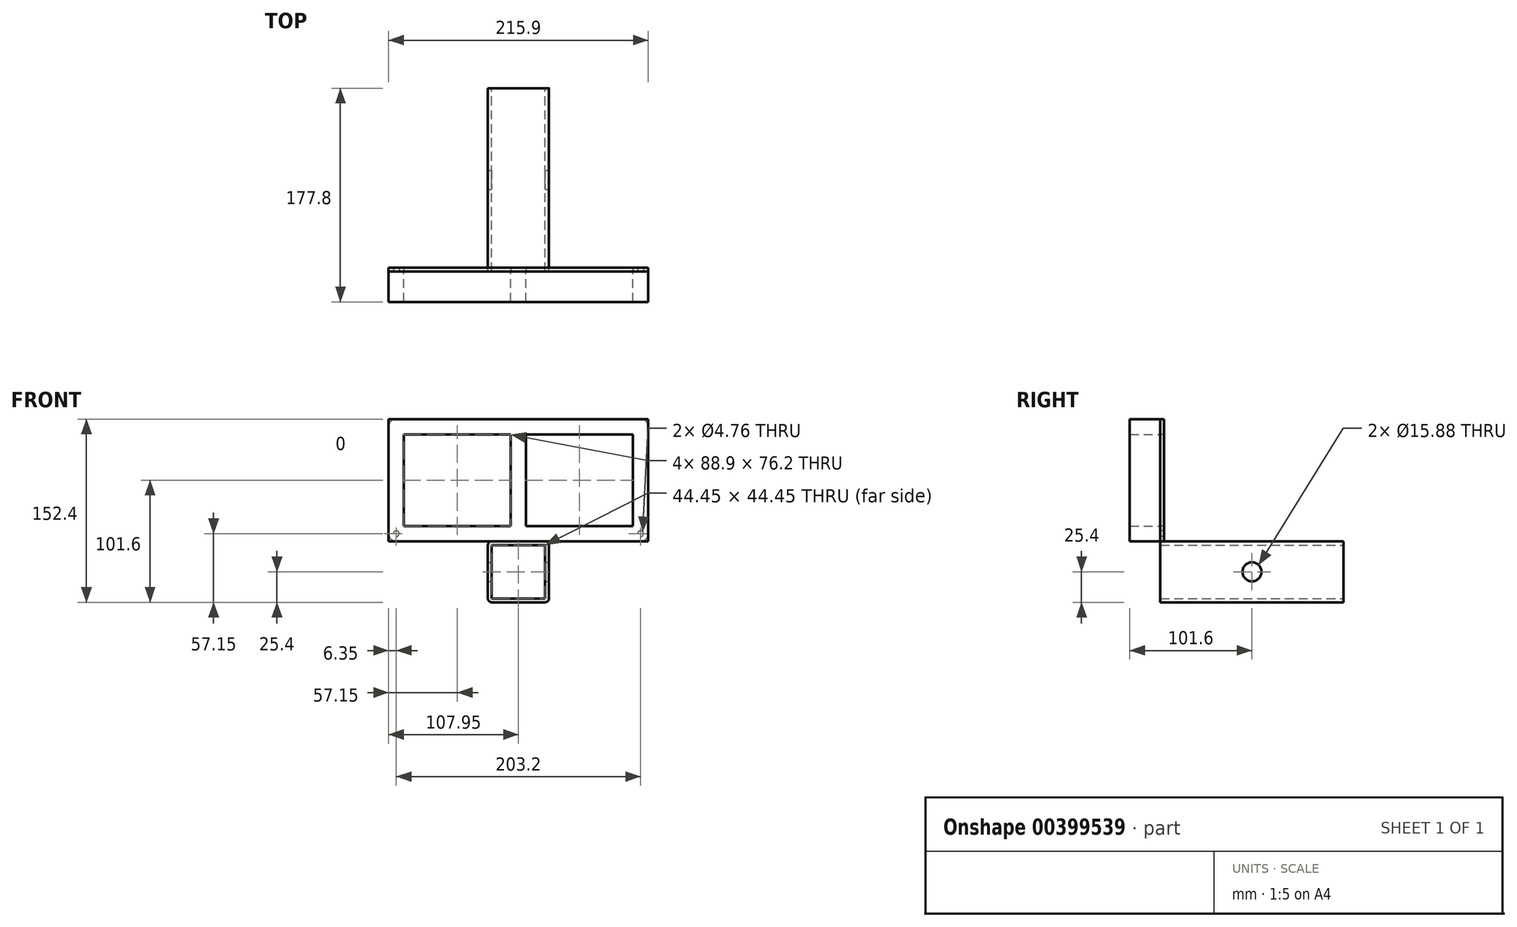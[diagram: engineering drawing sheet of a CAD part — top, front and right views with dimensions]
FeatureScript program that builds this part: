
annotation { "Feature Type Name" : "Feature", "Feature Type Description" : "" }
export const myFeature = defineFeature(function(context is Context, id is Id, definition is map)
    precondition{}
    {
        {
            var Q0;
            Q0=qCreatedBy(makeId("Front.planeOp"),FACE);
            var sketch = newSketch(context, id + "F0", { "sketchPlane" : qUnion([Q0])});
            skLineSegment(sketch, "E0.bottom", {"start": v(22.23, 25.4) * mm, "end": v(-22.23, 25.4) * mm});
            skLineSegment(sketch, "E0.top", {"start": v(22.23, -25.4) * mm, "end": v(-22.23, -25.4) * mm});
            skLineSegment(sketch, "E0.left", {"start": v(25.4, 22.23) * mm, "end": v(25.4, -22.22) * mm});
            skLineSegment(sketch, "E0.right", {"start": v(-25.4, 22.23) * mm, "end": v(-25.4, -22.23) * mm});
            skPoint(sketch, "E0.middle", {"position": v(0, 0) * mm});
            skLineSegment(sketch, "E1.0", {"start": v(22.23, 22.23) * mm, "end": v(-22.23, 22.23) * mm});
            skLineSegment(sketch, "E1.1", {"start": v(22.23, 22.23) * mm, "end": v(22.23, -22.22) * mm});
            skLineSegment(sketch, "E1.2", {"start": v(22.23, -22.22) * mm, "end": v(-22.23, -22.22) * mm});
            skLineSegment(sketch, "E1.3", {"start": v(-22.23, 22.23) * mm, "end": v(-22.23, -22.23) * mm});
            skPoint(sketch, "E2.visualSharp", {"position": v(-25.4, 25.4) * mm});
            skArc(sketch, "E2.filletArc", {"start": v(-22.23, 25.4) * mm, "mid": v(-24.47, 24.47) * mm, "end": v(-25.4, 22.23) * mm});
            skPoint(sketch, "E3.visualSharp", {"position": v(25.4, 25.4) * mm});
            skArc(sketch, "E3.filletArc", {"start": v(25.4, 22.23) * mm, "mid": v(24.47, 24.47) * mm, "end": v(22.23, 25.4) * mm});
            skPoint(sketch, "E4.visualSharp", {"position": v(25.4, -25.4) * mm});
            skArc(sketch, "E4.filletArc", {"start": v(22.23, -25.4) * mm, "mid": v(24.47, -24.47) * mm, "end": v(25.4, -22.22) * mm});
            skPoint(sketch, "E5.visualSharp", {"position": v(-25.4, -25.4) * mm});
            skArc(sketch, "E5.filletArc", {"start": v(-25.4, -22.23) * mm, "mid": v(-24.47, -24.47) * mm, "end": v(-22.23, -25.4) * mm});
            skSolve(sketch);
        }
        {
            var Q0;
            Q0=makeQuery(id+"F0.imprint","IMPRINT",FACE,{"disambiguationData":[TD([[makeQuery(id+"F0.imprint","IMPRINT",EDGE,{"derivedFrom":sQuery(id+"F0.wireOp",EDGE,"E0.bottom")}),1.0]])]});
            extrude(context, id + "F1", {"entities" : qUnion([Q0]), "depth" : 152.4 * mm});
        }
        {
            var Q0;
            Q0=makeQuery(id+"F1.opExtrude","SWEPT_FACE",FACE,{"disambiguationData":[OSD([sQuery(id+"F0.wireOp",EDGE,"E0.left")])]});
            var sketch = newSketch(context, id + "F2", { "sketchPlane" : qUnion([Q0])});
            skLineSegment(sketch, "E6", {"start": v(-152.4, 0) * mm, "end": v(-76.2, 0) * mm});
            skSolve(sketch);
        }
        {
            var Q0;
            Q0=sQuery(id+"F2.wireOp",VERTEX,"E6.end");
            var Q1;
            Q1=makeQuery(id+"F1.opExtrude","SWEPT_BODY",BODY,{"disambiguationData":[OSD([sQuery(id+"F0.wireOp",EDGE,"E0.bottom"),sQuery(id+"F0.wireOp",EDGE,"E0.top"),sQuery(id+"F0.wireOp",EDGE,"E0.left"),sQuery(id+"F0.wireOp",EDGE,"E0.right"),sQuery(id+"F0.wireOp",EDGE,"E1.0"),sQuery(id+"F0.wireOp",EDGE,"E1.1"),sQuery(id+"F0.wireOp",EDGE,"E1.2"),sQuery(id+"F0.wireOp",EDGE,"E1.3"),sQuery(id+"F0.wireOp",EDGE,"E2.filletArc"),sQuery(id+"F0.wireOp",EDGE,"E3.filletArc"),sQuery(id+"F0.wireOp",EDGE,"E4.filletArc"),sQuery(id+"F0.wireOp",EDGE,"E5.filletArc")])]});
            hole(context, id + "F3", {"style" : HoleStyle.SIMPLE, "endStyle" : HoleEndStyle.THROUGH, "holeDiameter" : 15.88 * mm, "locations" : qUnion([Q0]), "scope" : qUnion([Q1]), "isTappedThrough" : true});
        }
        {
            var Q0;
            Q0=makeQuery(id+"F1.opExtrude","CAP_FACE",FACE,{"disambiguationData":[OSD([sQuery(id+"F0.wireOp",EDGE,"E0.bottom"),sQuery(id+"F0.wireOp",EDGE,"E0.top"),sQuery(id+"F0.wireOp",EDGE,"E0.left"),sQuery(id+"F0.wireOp",EDGE,"E0.right"),sQuery(id+"F0.wireOp",EDGE,"E1.0"),sQuery(id+"F0.wireOp",EDGE,"E1.1"),sQuery(id+"F0.wireOp",EDGE,"E1.2"),sQuery(id+"F0.wireOp",EDGE,"E1.3"),sQuery(id+"F0.wireOp",EDGE,"E2.filletArc"),sQuery(id+"F0.wireOp",EDGE,"E3.filletArc"),sQuery(id+"F0.wireOp",EDGE,"E4.filletArc"),sQuery(id+"F0.wireOp",EDGE,"E5.filletArc")])],"isStart":false});
            var sketch = newSketch(context, id + "F4", { "sketchPlane" : qUnion([Q0])});
            skLineSegment(sketch, "E7", {"start": v(0, -1) * mm, "end": v(0, 25.4) * mm});
            skLineSegment(sketch, "E8", {"start": v(0, 25.4) * mm, "end": v(107.95, 25.4) * mm});
            skLineSegment(sketch, "E9", {"start": v(107.95, 25.4) * mm, "end": v(107.95, 127) * mm});
            skLineSegment(sketch, "E10.0", {"start": v(95.25, 38.1) * mm, "end": v(95.25, 114.3) * mm});
            skLineSegment(sketch, "E10.1", {"start": v(6.35, 38.1) * mm, "end": v(95.25, 38.1) * mm});
            skLineSegment(sketch, "E11", {"start": v(6.35, 38.1) * mm, "end": v(6.35, 114.3) * mm});
            skLineSegment(sketch, "E12.MirrorCS", {"start": v(0, 25.4) * mm, "end": v(-107.95, 25.4) * mm});
            skLineSegment(sketch, "E13.MirrorCS", {"start": v(-107.95, 25.4) * mm, "end": v(-107.95, 127) * mm});
            skLineSegment(sketch, "E14.MirrorCS", {"start": v(-95.25, 38.1) * mm, "end": v(-95.25, 114.3) * mm});
            skLineSegment(sketch, "E15.MirrorCS", {"start": v(-6.35, 38.1) * mm, "end": v(-95.25, 38.1) * mm});
            skLineSegment(sketch, "E16.MirrorCS", {"start": v(-6.35, 38.1) * mm, "end": v(-6.35, 114.3) * mm});
            skLineSegment(sketch, "E17", {"start": v(107.95, 127) * mm, "end": v(-107.95, 127) * mm});
            skLineSegment(sketch, "E18.0", {"start": v(95.25, 114.3) * mm, "end": v(6.35, 114.3) * mm});
            skLineSegment(sketch, "E19.trimOffspring", {"start": v(-6.35, 114.3) * mm, "end": v(-95.25, 114.3) * mm});
            skLineSegment(sketch, "E20", {"start": v(-107.95, 31.75) * mm, "end": v(107.95, 31.75) * mm, "construction": true});
            skPoint(sketch, "E21", {"position": v(-101.6, 31.75) * mm});
            skPoint(sketch, "E22", {"position": v(101.6, 31.75) * mm});
            skSolve(sketch);
        }
        {
            var Q0;
            {var subQ6=sQuery(id+"F4.wireOp",EDGE,"E9");Q0=makeQuery(id+"F4.imprint","IMPRINT",FACE,{"disambiguationData":[TD([[makeQuery(id+"F4.imprint","IMPRINT",EDGE,{"derivedFrom":subQ6}),1.0]])]});}
            extrude(context, id + "F5", {"entities" : qUnion([Q0]), "operationType" : NewBodyOperationType.ADD, "oppositeDirection" : true, "depth" : 3.17 * mm});
        }
        {
            var Q0;
            Q0=sQuery(id+"F4.wireOp",VERTEX,"E21");
            var Q1;
            Q1=sQuery(id+"F4.wireOp",VERTEX,"E22");
            var Q2;
            Q2=makeQuery(id+"F1.opExtrude","SWEPT_BODY",BODY,{"disambiguationData":[OSD([sQuery(id+"F0.wireOp",EDGE,"E0.bottom"),sQuery(id+"F0.wireOp",EDGE,"E0.top"),sQuery(id+"F0.wireOp",EDGE,"E0.left"),sQuery(id+"F0.wireOp",EDGE,"E0.right"),sQuery(id+"F0.wireOp",EDGE,"E1.0"),sQuery(id+"F0.wireOp",EDGE,"E1.1"),sQuery(id+"F0.wireOp",EDGE,"E1.2"),sQuery(id+"F0.wireOp",EDGE,"E1.3"),sQuery(id+"F0.wireOp",EDGE,"E2.filletArc"),sQuery(id+"F0.wireOp",EDGE,"E3.filletArc"),sQuery(id+"F0.wireOp",EDGE,"E4.filletArc"),sQuery(id+"F0.wireOp",EDGE,"E5.filletArc")])]});
            hole(context, id + "F6", {"style" : HoleStyle.SIMPLE, "endStyle" : HoleEndStyle.THROUGH, "holeDiameter" : 4.76 * mm, "locations" : qUnion([Q0, Q1]), "scope" : qUnion([Q2]), "isTappedThrough" : true});
        }
        {
            var Q0;
            Q0=makeQuery(id+"F5.opExtrude","SWEPT_EDGE",EDGE,{"disambiguationData":[OSD([sQuery(id+"F4.wireOp",EDGE,"E8"),sQuery(id+"F4.wireOp",EDGE,"E9")])]});
            var Q1;
            Q1=makeQuery(id+"F5.opExtrude","SWEPT_EDGE",EDGE,{"disambiguationData":[OSD([sQuery(id+"F4.wireOp",EDGE,"E9"),sQuery(id+"F4.wireOp",EDGE,"E17")])]});
            var Q2;
            Q2=makeQuery(id+"F5.opExtrude","SWEPT_EDGE",EDGE,{"disambiguationData":[OSD([sQuery(id+"F4.wireOp",EDGE,"E13.MirrorCS"),sQuery(id+"F4.wireOp",EDGE,"E17")])]});
            var Q3;
            Q3=makeQuery(id+"F5.opExtrude","SWEPT_EDGE",EDGE,{"disambiguationData":[OSD([sQuery(id+"F4.wireOp",EDGE,"E12.MirrorCS"),sQuery(id+"F4.wireOp",EDGE,"E13.MirrorCS")])]});
            fillet(context, id + "F7", {"entities" : qUnion([Q0, Q1, Q2, Q3]), "radius" : 6.35 * mm, "tangentPropagation" : true, "allowEdgeOverflow" : false});
        }
        {
            var Q0;
            {var subQ6=sQuery(id+"F4.wireOp",EDGE,"E9");Q0=makeQuery(id+"F4.imprint","IMPRINT",FACE,{"disambiguationData":[TD([[makeQuery(id+"F4.imprint","IMPRINT",EDGE,{"derivedFrom":subQ6}),1.0]])]});}
            extrude(context, id + "F8", {"entities" : qUnion([Q0]), "depth" : 25.4 * mm});
        }
    });
